# Revit family: Vitra-Sento-WashbasinCabinet-60872
name_source: partatom
category: Furniture Systems
units: mm (PartAtom-declared; Revit-internal decimal feet)

## family parameters
Cut with Voids When Loaded = No
Host = Face
OmniClass Number = 23.40.00.00
OmniClass Title = Equipment and Furnishings
Part Type = Normal
Room Calculation Point = No
Round Connector Dimension = Use Diameter
Shared = Yes

## types (1)
- Vitra_Sento Console, 95 cm, Light Oak_60872
    BIMobject category = Bathroom compound units
    Construction Type = Floor Mounted
    Default Elevation = 150 mm
    Depth = 400 mm  [stored 1.31234 ft]
    Description = Sento Console, 95 cm, Light Oak
    Design country = Turkey
    Height = 190 mm
    IFC Classification = Furniture
    Manufacturer = Vitra
    Manufacturer name = Vitra
    Masterformat 2014 Code = 13 42 13
    Masterformat 2014 Description = Bathroom Unit Modules
    Material main = Vitra-Light Oak
    Model = 60872
    NBS Reference Code = 35-75-08
    NBS Reference Description = Bathroom Cabinets
    Nominal height = 0 m³
    Nominal width = 0 m³
    OmniClass Code = 23-31 25 13
    OmniClass Description = Bathroom Cabinets
    Product Guid = https://cdn.vitra.com.tr
    Product SKU = 60872
    Product certification = https://vitraglobal.com
    Product data url = https://www.vitraglobal.com
    Product family = Sento
    Product group = Complementary Products
    Technical description = https://www.vitraglobal.com
    UNSPSC Code = 301815
    UNSPSC Description = Bathroom Cabinets
    URL = https://vitraglobal.com
    Uniclass 1.4 Code = L8241
    Uniclass 1.4 Description = Bathroom Cabinets
    Uniclass 2.0 Code = PR-35-75-08
    Uniclass 2.0 Description = Bathroom Cabinets
    Uniclass 2015 Code = Pr_40_20_93
    Uniclass 2015 Name = Wash basins, sinks and troughs
    Uniformat II Code = E20
    Uniformat II Description = FURNISHINGS
    Warranty Period (Year) = 2
    Weight Net (kg) = 6,500
    Width = 950 mm  [stored 3.1168 ft]
    Youtube = https://www.youtube.com

note: [stored X ft] marks values corroborated as IEEE doubles in the binary element streams (Revit-internal decimal feet)

## geometry (parser evidence)
native form markers: Sweep x3
no freeform markers — native parametric forms only
